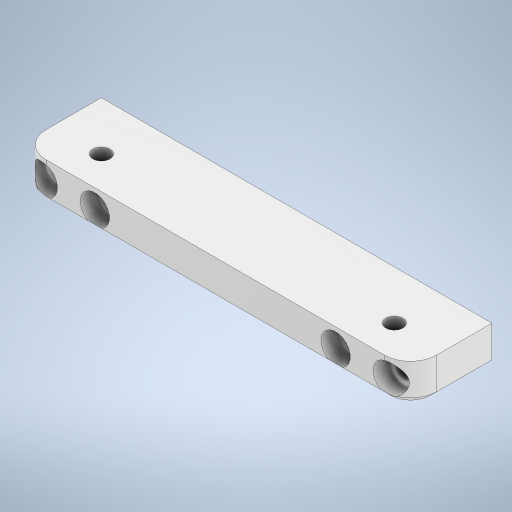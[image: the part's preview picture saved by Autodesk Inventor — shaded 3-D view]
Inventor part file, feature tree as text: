
AUTODESK INVENTOR PART (.ipt)
format: ipt  version: 2024 (Build 280153000, 153)  size: 327,680 bytes
history: native  units: mm
features: sketch x4, extrude x2, hole x2, fillet x1, chamfer x1, projected_geometry x1
ambient origin geometry x8: Origin, YZ Plane, XZ Plane, XY Plane, X Axis, Y Axis, Z Axis, Center Point
bodies: Solid1 (feature_tree)
feature tree (11):
  extrude  "Extrusion1"  Depth=11.75mm
  fillet  "Fillet1"  Radius=25.0mm
  chamfer  "Chamfer1"  Distance=2.0mm Angle=45.0deg
  hole  "Hole1"  [1 undecoded]
  hole  "Hole2"  [1 undecoded]
  extrude  "Extrusion2"  Depth=8.25mm
  sketch  "Sketch1"  dims[d0=120.0mm d1=11.75mm d2=25.0mm d3=0.0mm]
  sketch  "Sketch2"  dims[d4=8.0mm d5=2.0mm d6=2.0mm d7=45.0deg]
  sketch  "Sketch3"  dims[d8=16.0mm d9=6.0mm]
  sketch  "Sketch4"  dims[d15=5.3mm d16=6.0mm d17=9.0mm d18=5.0mm d19=90.0deg d20=8.0mm d21=20.594885mm d22=10.0mm d23=5.3mm d24=6.0mm d25=19.05mm d26=4.775mm d27=90.0deg d28=8.0mm d29=20.594885mm d30=8.25mm d31=5.0mm d32=0.0mm d35=15.0mm d36=15.0mm d37=90.0mm]
  projected_geometry  "Projected Loop1"
note: 2 required parameter values undecoded (feature->parameter linkage not recoverable at this tier; creation-order binding heuristic only, values carry confidence <= 0.55)
